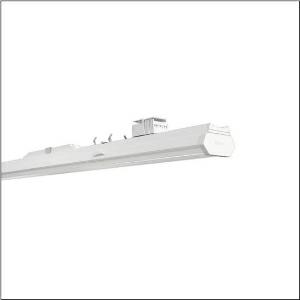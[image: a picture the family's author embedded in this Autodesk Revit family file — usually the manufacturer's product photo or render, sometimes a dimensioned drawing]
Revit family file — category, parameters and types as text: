
# Revit family: licross_r__21_protected_ho_52tp12dn4e5m3c_6a60
name_source: partatom
category: Lighting Fixtures
units: mm (PartAtom-declared; Revit-internal decimal feet)

## family parameters
Cut with Voids When Loaded = No
Host = Face
Light Source = No
Part Type = Normal
Room Calculation Point = No
Round Connector Dimension = Use Diameter
Shared = No

## types (1)
- --- (1 x LED, 910 lm, 7.6 W, 4000K)
    Apparent Load = 8 VA
    CIE Flux Codes = 70 91 97 98 100
    Color Rendering = 80
    Color Temperature = 4000K
    Default Elevation = 1800 mm
    Description = Licross® 21 Protected HO, luminaire insert, of sheet steel, galvanised, coil coated, white, length: 1.500mm, width: 90mm, height: 103mm, LED rated luminous flux: 14.690lm, light colour: 840, control gear: DALI 2 (for two DALI lines), with plug, 6-pole, with phase selection, for trunking rail, 14-core, mains connection: 220..240V, AC, 50/60Hz, rated input power: 89W, for trunking rail, 14-core, halogen-free wiring, for emergency light function, converter,control gear: single battery element, battery: LiFePO4, 9Ah, primary light control with lens, of plastic, primary optical cover: cover, of PMMA, light emission: direct distribution, primary light characteristic: symmetric, protection rating (complete): IP64, insulation class (complete): insulation class I (protective earthing), certification: CE, UKCA, protection symbol: D if used in an environment with conductive dust loads with corresponding accessories, impact resistance: IK06, permissible ambient temperature for indoor applications: +5..+30°C, standard: EN 60598-2-22, LABS conformity tested according to VDMA 24364:2018-05, reducing of maximum allowable ambient temperature of 5°C with ceiling mounting, corresponds to IFS (International Featured Standards) requirements for safety and quality in the food industry, packaging unit: 1 piece
    Height = 92 mm
    Lamp = 1 x LED
    Lamp Light Flux = 910 lm
    Lamp Power = 7.6 W
    Lamp count = 1
    Length = 1500 mm
    Luminous efficacy = 120 lm/W
    Manufacturer = Siteco
    ModVariant = No
    Model = 52TP12DN4E5M3C
    Mounting Place = Ceiling
    Mounting Type = Pendant
    Number of Poles = 1
    OnlyDefault = Yes
    Power Factor = 1
    Product Name = Licross® 21 Protected HO
    Product group = luminaire insert
    ProductGroupID = 902
    Protection Class = Protection class I
    Protection Degree = IP 64
    RLX_Detail_Level = 1
    RLX_Emergency_Light_Flux = 0 lm
    RLX_Emergency_Type = 0
    RLX_Emergency_Type_DB = No
    RlxData = <blob elided: 24921 chars, md5=598d3940>
    Socket = socket
    Standby Power = 0 W
    System Light Flux = 910 lm
    System Power = 8 W
    Type Comments = : emergency light operation: 3 h
    Type Image = l_1256148.jpg
    URL = http://relux.com
    VarID = @adj_111226
    Voltage = 0 V
    Weight = 0.00 kg
    Width = 88 mm

## geometry (parser evidence)
native form markers: Blend x4, Sweep x9
no freeform markers — native parametric forms only
